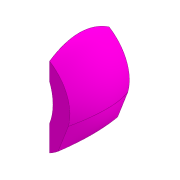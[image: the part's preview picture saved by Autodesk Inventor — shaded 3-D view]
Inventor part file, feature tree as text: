
AUTODESK INVENTOR PART (.ipt)
format: ipt  version: 2020 (Build 240168000, 168)  size: 929,280 bytes
history: native  units: mm
features: sketch x7, extrude x4, plane x3, other x3, loft x1, direct_edit x1, projected_geometry x1
ambient origin geometry x8: Origin, YZ Plane, XZ Plane, XY Plane, X Axis, Y Axis, Z Axis, Center Point
bodies: Solid1 (feature_tree)
feature tree (20):
  sketch  "Sketch1"  dims[d16=4.5mm d17=4.5mm]
  plane  "Work Plane1"
  sketch  "Sketch2"  dims[d19=0.0mm d20=90.0deg d21=0.0mm d22=90.0deg]
  plane  "Work Plane2"
  loft  "Loft1"
  extrude  "Extrusion1"  TaperAngle=0.0deg  [1 undecoded]
  plane  "Work Plane3"
  extrude  "Extrusion2"  Depth=0.2mm
  extrude  "Extrusion3"  Depth=10.0mm
  direct_edit  "Direct Edit1"
  extrude  "Extrusion4"  Depth=10.0mm TaperAngle=0.0deg
  other  "Image1"
  sketch  "Sketch3"  dims[d23=0.0mm d24=90.0deg d32=0.2mm]
  sketch  "Sketch4"  dims[d34=10.0mm d35=0.0mm d36=5.0mm]
  other  "Image2"
  sketch  "Sketch5"  dims[d37=10.0mm d38=0.0mm d39=4.5mm d40=0.0mm]
  projected_geometry  "Projected Loop1"
  sketch  "Sketch6"  dims[d41=8.0mm d42=10.0mm d43=10.0mm]
  sketch  "Sketch7"  dims[d44=10.0mm d45=0.0mm d33=0.5mm]
  other  "Scale1"
note: 1 required parameter value undecoded (feature->parameter linkage not recoverable at this tier; creation-order binding heuristic only, values carry confidence <= 0.55)
